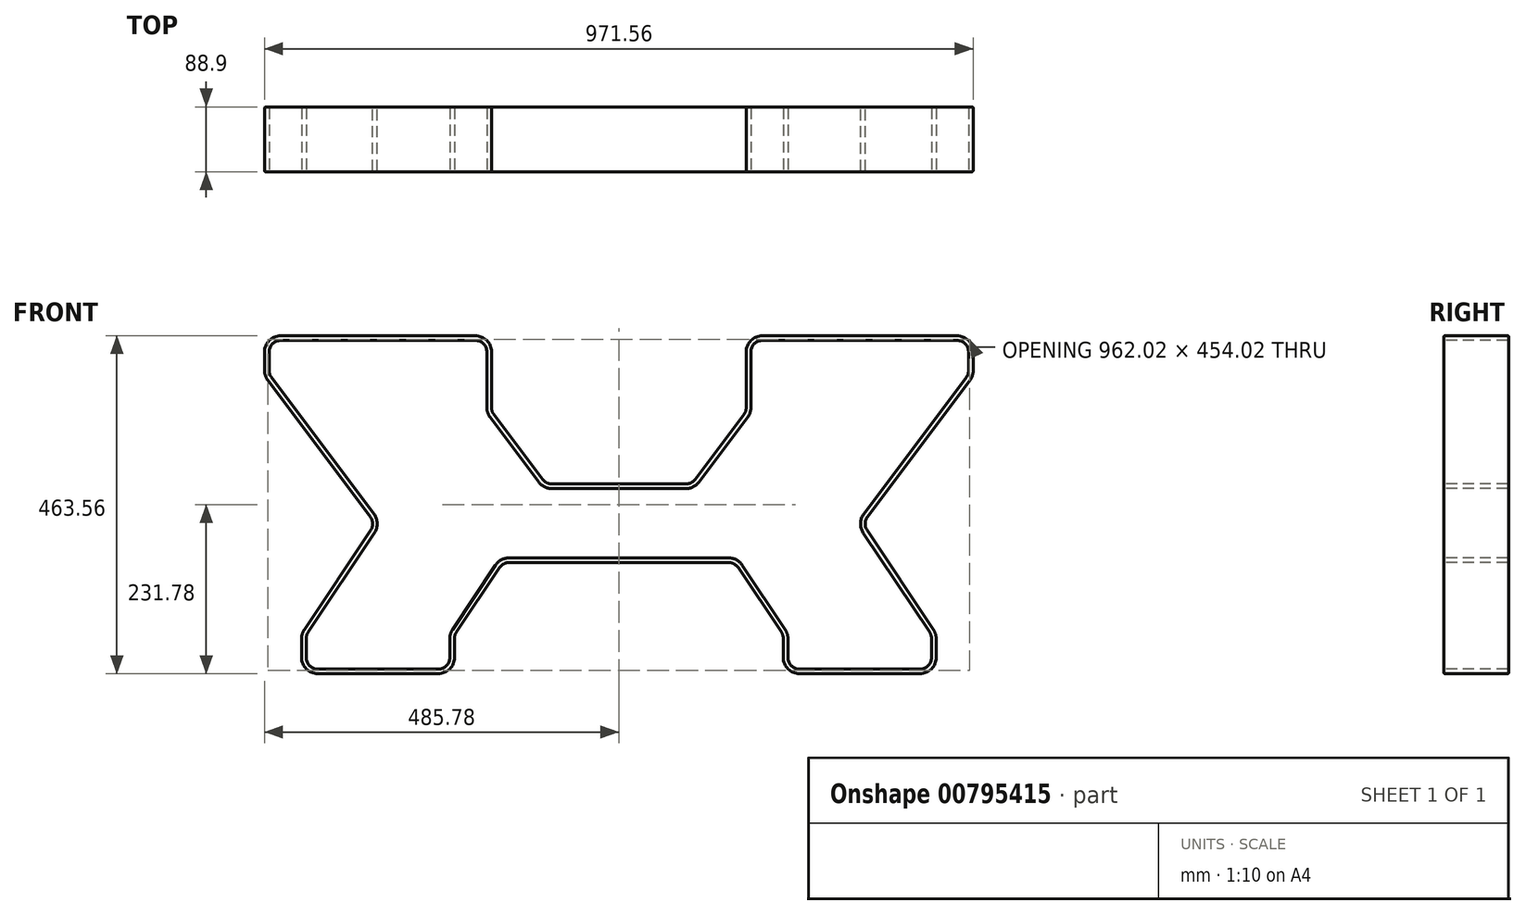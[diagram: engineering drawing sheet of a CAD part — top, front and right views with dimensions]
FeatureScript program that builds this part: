
annotation { "Feature Type Name" : "Feature", "Feature Type Description" : "" }
export const myFeature = defineFeature(function(context is Context, id is Id, definition is map)
    precondition{}
    {
        {
            var Q0;
            Q0=qCreatedBy(makeId("Front.planeOp"),FACE);
            var sketch = newSketch(context, id + "F0", { "sketchPlane" : qUnion([Q0])});
            skLineSegment(sketch, "E0", {"start": v(0, 0) * mm, "end": v(-92.07, 0) * mm});
            skLineSegment(sketch, "E1", {"start": v(-107.31, 7.62) * mm, "end": v(-173.99, 96.52) * mm});
            skLineSegment(sketch, "E2", {"start": v(-177.8, 107.95) * mm, "end": v(-177.8, 184.15) * mm});
            skLineSegment(sketch, "E3", {"start": v(-196.85, 203.2) * mm, "end": v(-463.55, 203.2) * mm});
            skLineSegment(sketch, "E4", {"start": v(-482.6, 184.15) * mm, "end": v(-482.6, 158.75) * mm});
            skLineSegment(sketch, "E5", {"start": v(-478.79, 147.32) * mm, "end": v(-338.29, -40.02) * mm});
            skLineSegment(sketch, "E6", {"start": v(-337.68, -62.01) * mm, "end": v(-428.6, -198.4) * mm});
            skLineSegment(sketch, "E7", {"start": v(-431.8, -208.97) * mm, "end": v(-431.8, -234.95) * mm});
            skLineSegment(sketch, "E8", {"start": v(-412.75, -254) * mm, "end": v(-247.65, -254) * mm});
            skLineSegment(sketch, "E9", {"start": v(-228.6, -234.95) * mm, "end": v(-228.6, -208.97) * mm});
            skLineSegment(sketch, "E10", {"start": v(-225.4, -198.4) * mm, "end": v(-166.52, -110.08) * mm});
            skLineSegment(sketch, "E11", {"start": v(-150.67, -101.6) * mm, "end": v(0, -101.6) * mm});
            skPoint(sketch, "E12.visualSharp", {"position": v(-177.8, 203.2) * mm});
            skArc(sketch, "E12.filletArc", {"start": v(-177.8, 184.15) * mm, "mid": v(-183.38, 197.62) * mm, "end": v(-196.85, 203.2) * mm});
            skPoint(sketch, "E13.visualSharp", {"position": v(-482.6, 203.2) * mm});
            skArc(sketch, "E13.filletArc", {"start": v(-463.55, 203.2) * mm, "mid": v(-477.02, 197.62) * mm, "end": v(-482.6, 184.15) * mm});
            skPoint(sketch, "E14.visualSharp", {"position": v(-482.6, 152.4) * mm});
            skArc(sketch, "E14.filletArc", {"start": v(-482.6, 158.75) * mm, "mid": v(-481.62, 152.73) * mm, "end": v(-478.79, 147.32) * mm});
            skPoint(sketch, "E15.visualSharp", {"position": v(-330.2, -50.8) * mm});
            skArc(sketch, "E15.filletArc", {"start": v(-337.68, -62.01) * mm, "mid": v(-334.48, -50.92) * mm, "end": v(-338.29, -40.02) * mm});
            skPoint(sketch, "E16.visualSharp", {"position": v(-431.8, -203.2) * mm});
            skArc(sketch, "E16.filletArc", {"start": v(-428.6, -198.4) * mm, "mid": v(-430.98, -203.45) * mm, "end": v(-431.8, -208.97) * mm});
            skPoint(sketch, "E17.visualSharp", {"position": v(-431.8, -254) * mm});
            skArc(sketch, "E17.filletArc", {"start": v(-431.8, -234.95) * mm, "mid": v(-426.22, -248.42) * mm, "end": v(-412.75, -254) * mm});
            skPoint(sketch, "E18.visualSharp", {"position": v(-228.6, -254) * mm});
            skArc(sketch, "E18.filletArc", {"start": v(-247.65, -254) * mm, "mid": v(-234.18, -248.42) * mm, "end": v(-228.6, -234.95) * mm});
            skPoint(sketch, "E19.visualSharp", {"position": v(-228.6, -203.2) * mm});
            skArc(sketch, "E19.filletArc", {"start": v(-225.4, -198.4) * mm, "mid": v(-227.78, -203.45) * mm, "end": v(-228.6, -208.97) * mm});
            skPoint(sketch, "E20.visualSharp", {"position": v(-160.87, -101.6) * mm});
            skArc(sketch, "E20.filletArc", {"start": v(-150.67, -101.6) * mm, "mid": v(-159.66, -103.85) * mm, "end": v(-166.52, -110.08) * mm});
            skPoint(sketch, "E21.visualSharp", {"position": v(-101.6, 0) * mm});
            skArc(sketch, "E21.filletArc", {"start": v(-107.31, 7.62) * mm, "mid": v(-100.6, 2.01) * mm, "end": v(-92.07, 0) * mm});
            skPoint(sketch, "E22.visualSharp", {"position": v(-177.8, 101.6) * mm});
            skArc(sketch, "E22.filletArc", {"start": v(-177.8, 107.95) * mm, "mid": v(-176.82, 101.93) * mm, "end": v(-173.99, 96.52) * mm});
            skSolve(sketch);
        }
        {
            var Q0;
            Q0=qCreatedBy(makeId("Right.planeOp"),FACE);
            var sketch = newSketch(context, id + "F1", { "sketchPlane" : qUnion([Q0])});
            skLineSegment(sketch, "E23.bottom", {"start": v(42.86, -3.17) * mm, "end": v(-42.86, -3.18) * mm});
            skLineSegment(sketch, "E23.top", {"start": v(42.86, 3.18) * mm, "end": v(-42.86, 3.17) * mm});
            skLineSegment(sketch, "E23.left", {"start": v(44.45, -1.59) * mm, "end": v(44.45, 1.59) * mm});
            skLineSegment(sketch, "E23.right", {"start": v(-44.45, -1.59) * mm, "end": v(-44.45, 1.59) * mm});
            skPoint(sketch, "E23.middle", {"position": v(0, 0) * mm});
            skPoint(sketch, "E24.visualSharp", {"position": v(-44.45, 3.17) * mm});
            skArc(sketch, "E24.filletArc", {"start": v(-42.86, 3.17) * mm, "mid": v(-43.99, 2.71) * mm, "end": v(-44.45, 1.59) * mm});
            skPoint(sketch, "E25.visualSharp", {"position": v(-44.45, -3.18) * mm});
            skArc(sketch, "E25.filletArc", {"start": v(-44.45, -1.59) * mm, "mid": v(-43.99, -2.71) * mm, "end": v(-42.86, -3.18) * mm});
            skPoint(sketch, "E26.visualSharp", {"position": v(44.45, 3.18) * mm});
            skArc(sketch, "E26.filletArc", {"start": v(44.45, 1.59) * mm, "mid": v(43.99, 2.71) * mm, "end": v(42.86, 3.18) * mm});
            skPoint(sketch, "E27.visualSharp", {"position": v(44.45, -3.17) * mm});
            skArc(sketch, "E27.filletArc", {"start": v(42.86, -3.17) * mm, "mid": v(43.99, -2.71) * mm, "end": v(44.45, -1.59) * mm});
            skSolve(sketch);
        }
        {
            var Q0;
            Q0=makeQuery(id+"F1.imprint","IMPRINT",FACE,{"disambiguationData":[TD([[makeQuery(id+"F1.imprint","IMPRINT",EDGE,{"derivedFrom":sQuery(id+"F1.wireOp",EDGE,"E23.bottom")}),-1.0]])]});
            var Q1;
            Q1=sQuery(id+"F0.wireOp",EDGE,"E11");
            var Q2;
            Q2=sQuery(id+"F0.wireOp",EDGE,"E10");
            var Q3;
            Q3=sQuery(id+"F0.wireOp",EDGE,"E8");
            var Q4;
            Q4=sQuery(id+"F0.wireOp",EDGE,"E6");
            var Q5;
            Q5=sQuery(id+"F0.wireOp",EDGE,"E5");
            var Q6;
            Q6=sQuery(id+"F0.wireOp",EDGE,"E3");
            var Q7;
            Q7=sQuery(id+"F0.wireOp",EDGE,"E2");
            var Q8;
            Q8=sQuery(id+"F0.wireOp",EDGE,"E1");
            var Q9;
            Q9=sQuery(id+"F0.wireOp",EDGE,"E0");
            var Q10;
            Q10=sQuery(id+"F0.wireOp",EDGE,"E9");
            var Q11;
            Q11=sQuery(id+"F0.wireOp",EDGE,"E7");
            var Q12;
            Q12=sQuery(id+"F0.wireOp",EDGE,"E17.filletArc");
            var Q13;
            Q13=sQuery(id+"F0.wireOp",EDGE,"E18.filletArc");
            var Q14;
            Q14=sQuery(id+"F0.wireOp",EDGE,"E13.filletArc");
            var Q15;
            Q15=sQuery(id+"F0.wireOp",EDGE,"E4");
            var Q16;
            Q16=sQuery(id+"F0.wireOp",EDGE,"E14.filletArc");
            var Q17;
            Q17=sQuery(id+"F0.wireOp",EDGE,"E12.filletArc");
            var Q18;
            Q18=sQuery(id+"F0.wireOp",EDGE,"E22.filletArc");
            var Q19;
            Q19=sQuery(id+"F0.wireOp",EDGE,"E15.filletArc");
            var Q20;
            Q20=sQuery(id+"F0.wireOp",EDGE,"E21.filletArc");
            var Q21;
            Q21=sQuery(id+"F0.wireOp",EDGE,"E20.filletArc");
            var Q22;
            Q22=sQuery(id+"F0.wireOp",EDGE,"E19.filletArc");
            var Q23;
            Q23=sQuery(id+"F0.wireOp",EDGE,"E16.filletArc");
            sweep(context, id + "F2", {"profiles" : qUnion([Q0]), "path" : qUnion([Q1, Q2, Q3, Q4, Q5, Q6, Q7, Q8, Q9, Q10, Q11, Q12, Q13, Q14, Q15, Q16, Q17, Q18, Q19, Q20, Q21, Q22, Q23])});
        }
        {
            var Q0;
            Q0=makeQuery(id+"F2.opSweep","SWEPT_BODY",BODY,{"disambiguationData":[OSD([sQuery(id+"F0.wireOp",EDGE,"E15.filletArc"),sQuery(id+"F1.wireOp",EDGE,"E23.bottom"),sQuery(id+"F1.wireOp",EDGE,"E23.top"),sQuery(id+"F1.wireOp",EDGE,"E23.left"),sQuery(id+"F1.wireOp",EDGE,"E23.right"),sQuery(id+"F1.wireOp",EDGE,"E24.filletArc"),sQuery(id+"F1.wireOp",EDGE,"E25.filletArc"),sQuery(id+"F1.wireOp",EDGE,"E26.filletArc"),sQuery(id+"F1.wireOp",EDGE,"E27.filletArc")])]});
            var Q1;
            Q1=qCreatedBy(makeId("Right.planeOp"),FACE);
            mirror(context, id + "F3", {"operationType" : NewBodyOperationType.ADD, "entities" : qUnion([Q0]), "mirrorPlane" : qUnion([Q1])});
        }
    });
